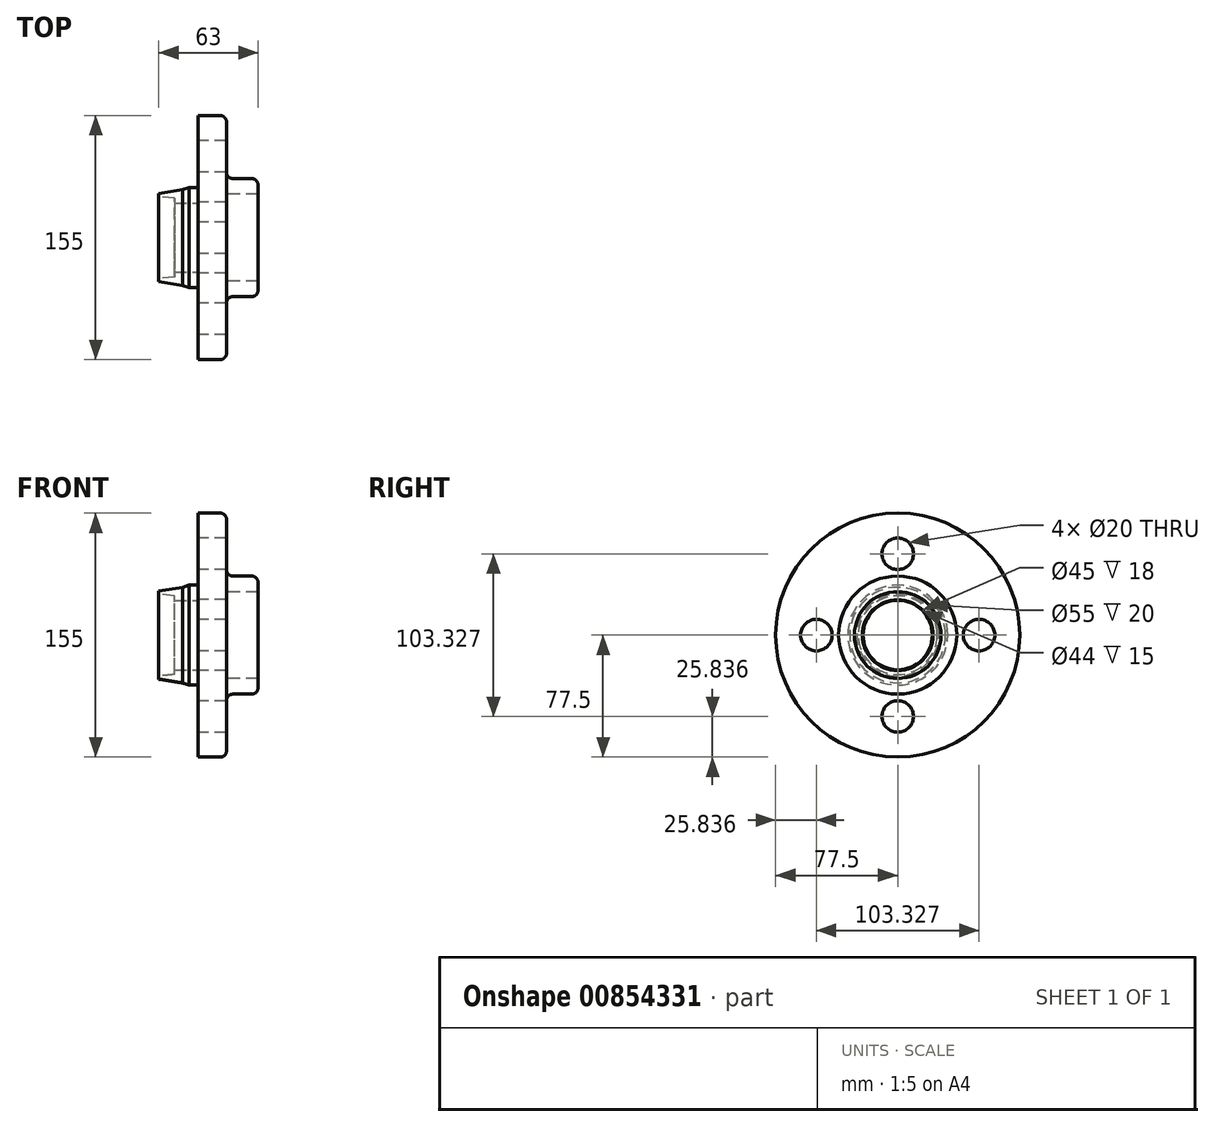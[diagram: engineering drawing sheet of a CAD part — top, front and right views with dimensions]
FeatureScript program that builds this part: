
annotation { "Feature Type Name" : "Feature", "Feature Type Description" : "" }
export const myFeature = defineFeature(function(context is Context, id is Id, definition is map)
    precondition{}
    {
        {
            var Q0;
            Q0=qCreatedBy(makeId("Right.planeOp"),FACE);
            var sketch = newSketch(context, id + "F0", { "sketchPlane" : qUnion([Q0])});
            skCircle(sketch, "E0", {"center": v(0, 0) * mm, "radius": 77.5 * mm});
            skCircle(sketch, "E1", {"center": v(0, 0) * mm, "radius": 22.5 * mm});
            skSolve(sketch);
        }
        {
            var Q0;
            Q0=makeQuery(id+"F0.imprint","IMPRINT",FACE,{"disambiguationData":[TD([[makeQuery(id+"F0.imprint","IMPRINT",EDGE,{"derivedFrom":sQuery(id+"F0.wireOp",EDGE,"E0")}),1.0]])]});
            extrude(context, id + "F1", {"entities" : qUnion([Q0]), "depth" : 18 * mm, "offsetDistance" : 25 * mm});
        }
        {
            var Q0;
            Q0=makeQuery(id+"F1.opExtrude","CAP_FACE",FACE,{"disambiguationData":[OSD([sQuery(id+"F0.wireOp",EDGE,"E0"),sQuery(id+"F0.wireOp",EDGE,"E1")])],"isStart":false});
            var sketch = newSketch(context, id + "F2", { "sketchPlane" : qUnion([Q0])});
            skCircle(sketch, "E2", {"center": v(0, 0) * mm, "radius": 37.5 * mm});
            skCircle(sketch, "E3", {"center": v(0, 0) * mm, "radius": 27.5 * mm});
            skSolve(sketch);
        }
        {
            var Q0;
            Q0 = qSketchRegion(id + "F2", true);
            extrude(context, id + "F3", {"entities" : qUnion([Q0]), "operationType" : NewBodyOperationType.ADD, "depth" : 20 * mm, "offsetDistance" : 25 * mm});
        }
        {
            var Q0;
            Q0=makeQuery(id+"F3.opExtrude","SWEPT_FACE",FACE,{"disambiguationData":[OSD([sQuery(id+"F2.wireOp",EDGE,"E2")])]});
            var Q1;
            Q1=makeQuery(id+"F1.opExtrude","CAP_EDGE",EDGE,{"disambiguationData":[OSD([sQuery(id+"F0.wireOp",EDGE,"E0")])],"isStart":false});
            fillet(context, id + "F4", {"entities" : qUnion([Q0, Q1]), "radius" : 4 * mm, "tangentPropagation" : true, "allowEdgeOverflow" : false});
        }
        {
            var Q0;
            Q0=qCreatedBy(makeId("Front.planeOp"),FACE);
            var sketch = newSketch(context, id + "F5", { "sketchPlane" : qUnion([Q0])});
            skLineSegment(sketch, "E4", {"start": v(0, -31.75) * mm, "end": v(-5.72, -31.75) * mm});
            skLineSegment(sketch, "E5", {"start": v(-5.72, -31.75) * mm, "end": v(-10, -30.35) * mm});
            skLineSegment(sketch, "E6", {"start": v(-10, -30.35) * mm, "end": v(-25, -28) * mm});
            skLineSegment(sketch, "E7", {"start": v(-25, -28) * mm, "end": v(-25, -26) * mm});
            skLineSegment(sketch, "E8", {"start": v(-25, -26) * mm, "end": v(-15, -25) * mm});
            skLineSegment(sketch, "E9", {"start": v(-15, -25) * mm, "end": v(-15, -22) * mm});
            skLineSegment(sketch, "E10", {"start": v(-15, -22) * mm, "end": v(0, -22) * mm});
            skLineSegment(sketch, "E11", {"start": v(0, -22) * mm, "end": v(0, -31.75) * mm});
            skLineSegment(sketch, "E12", {"start": v(0, 0) * mm, "end": v(-15, 0) * mm, "construction": true});
            skSolve(sketch);
        }
        {
            var Q0;
            Q0 = qSketchRegion(id + "F5", true);
            var Q1;
            Q1=sQuery(id+"F5.wireOp",EDGE,"E12");
            revolve(context, id + "F6", {"operationType" : NewBodyOperationType.ADD, "surfaceOperationType" : NewSurfaceOperationType.NEW, "entities" : qUnion([Q0]), "axis" : qUnion([Q1]), "revolveType" : RevolveType.FULL});
        }
        {
            var Q0;
            Q0=qCreatedBy(makeId("Right.planeOp"),FACE);
            var sketch = newSketch(context, id + "F7", { "sketchPlane" : qUnion([Q0])});
            skCircle(sketch, "E13", {"center": v(0, 51.66) * mm, "radius": 10 * mm});
            skCircle(sketch, "E14", {"center": v(0, 0) * mm, "radius": 51.66 * mm, "construction": true});
            skCircle(sketch, "E15", {"center": v(51.66, 0) * mm, "radius": 10 * mm});
            skCircle(sketch, "E16", {"center": v(-51.66, 0) * mm, "radius": 10 * mm});
            skCircle(sketch, "E17", {"center": v(0, -51.66) * mm, "radius": 10 * mm});
            skSolve(sketch);
        }
        {
            var Q0;
            Q0=makeQuery(id+"F7.imprint","IMPRINT",FACE,{"disambiguationData":[TD([[makeQuery(id+"F7.imprint","IMPRINT",EDGE,{"derivedFrom":sQuery(id+"F7.wireOp",EDGE,"E13")}),1.0]])]});
            var Q1;
            Q1=makeQuery(id+"F7.imprint","IMPRINT",FACE,{"disambiguationData":[TD([[makeQuery(id+"F7.imprint","IMPRINT",EDGE,{"derivedFrom":sQuery(id+"F7.wireOp",EDGE,"E16")}),1.0]])]});
            var Q2;
            Q2=makeQuery(id+"F7.imprint","IMPRINT",FACE,{"disambiguationData":[TD([[makeQuery(id+"F7.imprint","IMPRINT",EDGE,{"derivedFrom":sQuery(id+"F7.wireOp",EDGE,"E17")}),1.0]])]});
            var Q3;
            Q3=makeQuery(id+"F7.imprint","IMPRINT",FACE,{"disambiguationData":[TD([[makeQuery(id+"F7.imprint","IMPRINT",EDGE,{"derivedFrom":sQuery(id+"F7.wireOp",EDGE,"E15")}),1.0]])]});
            extrude(context, id + "F8", {"entities" : qUnion([Q0, Q1, Q2, Q3]), "operationType" : NewBodyOperationType.REMOVE, "depth" : 25 * mm, "offsetDistance" : 25 * mm});
        }
    });
